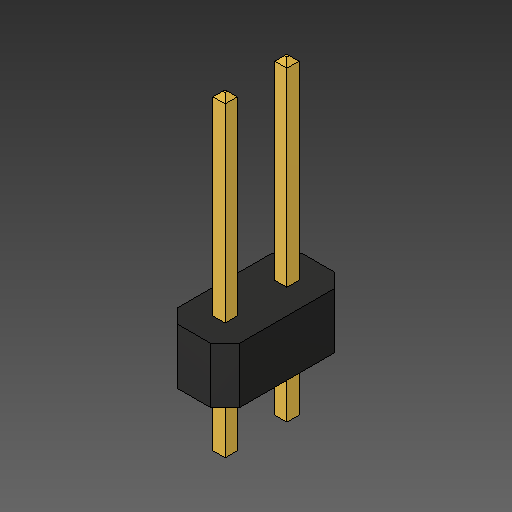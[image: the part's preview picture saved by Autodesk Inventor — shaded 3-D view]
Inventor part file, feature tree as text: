
AUTODESK INVENTOR PART (.ipt)
format: ipt  version: 2018.2 (Build 222227000, 227)  size: 108,544 bytes
history: native  units: mm
features: other x1, chamfer x1
ambient origin geometry x8: Origin, YZ Plane, XZ Plane, XY Plane, X Axis, Y Axis, Z Axis, Center Point
bodies: Body1 (feature_tree)
feature tree (2):
  other  "ソリッド1"
  chamfer  "Chamfer2"  [1 undecoded]
note: 1 required parameter value undecoded (feature->parameter linkage not recoverable at this tier; creation-order binding heuristic only, values carry confidence <= 0.55)
